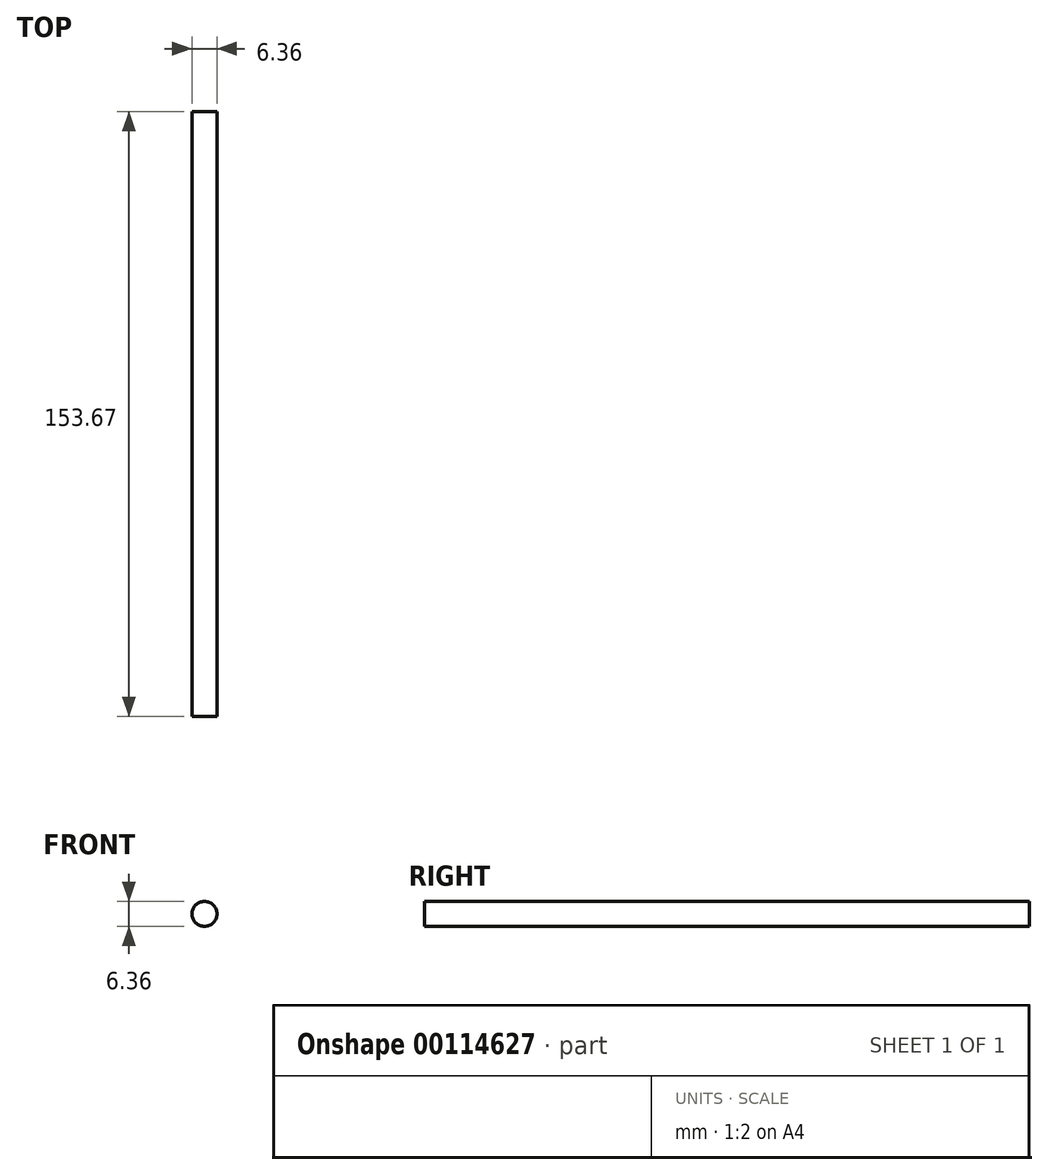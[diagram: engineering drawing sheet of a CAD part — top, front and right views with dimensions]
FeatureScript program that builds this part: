
annotation { "Feature Type Name" : "Feature", "Feature Type Description" : "" }
export const myFeature = defineFeature(function(context is Context, id is Id, definition is map)
    precondition{}
    {
        {
            var Q0;
            Q0=qCreatedBy(makeId("Front.planeOp"),FACE);
            var sketch = newSketch(context, id + "F0", { "sketchPlane" : qUnion([Q0])});
            skCircle(sketch, "E0", {"center": v(0, 0) * mm, "radius": 3.18 * mm});
            skSolve(sketch);
        }
        {
            var Q0;
            Q0 = qSketchRegion(id + "F0", true);
            extrude(context, id + "F1", {"entities" : qUnion([Q0]), "depth" : 153.67 * mm});
        }
    });
